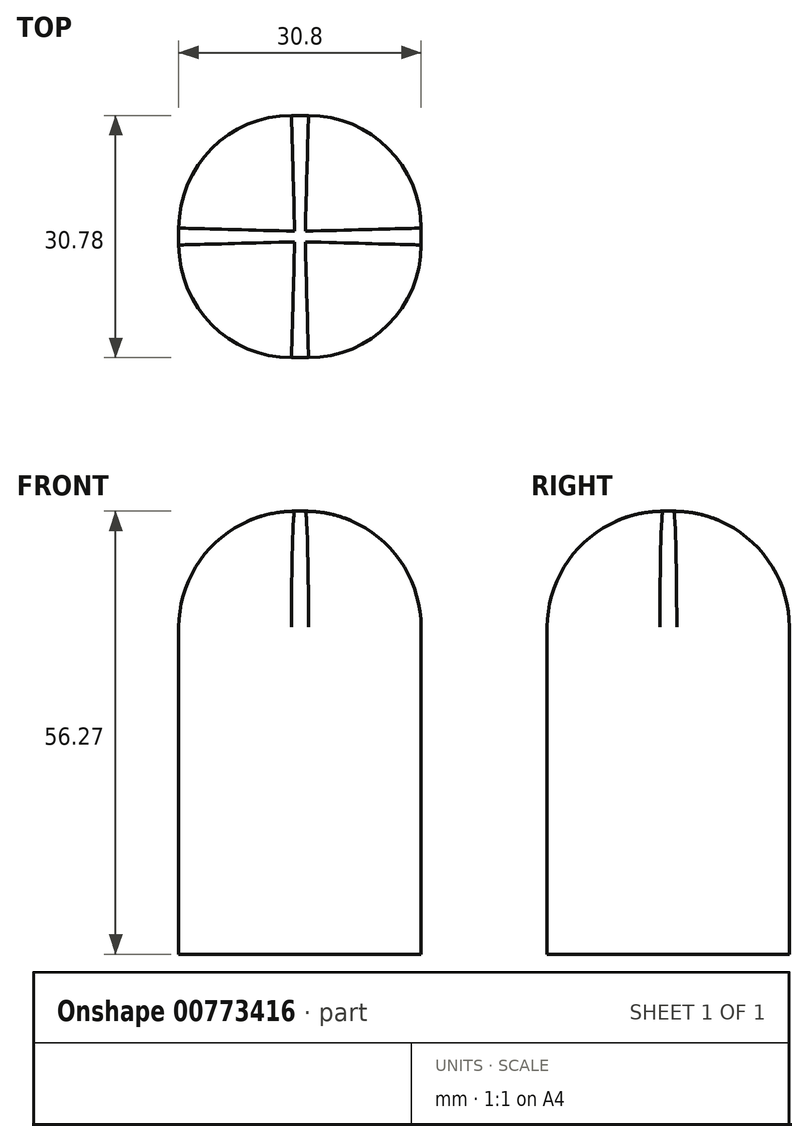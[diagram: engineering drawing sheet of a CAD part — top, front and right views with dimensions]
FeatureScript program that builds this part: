
annotation { "Feature Type Name" : "Feature", "Feature Type Description" : "" }
export const myFeature = defineFeature(function(context is Context, id is Id, definition is map)
    precondition{}
    {
        {
            var Q0;
            Q0=qCreatedBy(makeId("Front.planeOp"),FACE);
            var sketch = newSketch(context, id + "F0", { "sketchPlane" : qUnion([Q0])});
            skLineSegment(sketch, "E0", {"start": v(0, 0) * mm, "end": v(0, 56.27) * mm});
            skLineSegment(sketch, "E1", {"start": v(0, 56.27) * mm, "end": v(15.4, 56.27) * mm});
            skLineSegment(sketch, "E2", {"start": v(15.4, 56.27) * mm, "end": v(15.4, 0) * mm});
            skLineSegment(sketch, "E3", {"start": v(15.4, 0) * mm, "end": v(0, 0) * mm});
            skLineSegment(sketch, "E4", {"start": v(0, 0) * mm, "end": v(-15.4, 0) * mm});
            skLineSegment(sketch, "E5", {"start": v(-15.4, 0) * mm, "end": v(-15.4, 56.27) * mm});
            skLineSegment(sketch, "E6", {"start": v(-15.4, 56.27) * mm, "end": v(0, 56.27) * mm});
            skSolve(sketch);
        }
        {
            var Q0;
            Q0=makeQuery(id+"F0.imprint","IMPRINT",FACE,{"disambiguationData":[TD([[makeQuery(id+"F0.imprint","IMPRINT",EDGE,{"derivedFrom":sQuery(id+"F0.wireOp",EDGE,"E0")}),1.0]])]});
            var Q1;
            Q1=makeQuery(id+"F0.imprint","IMPRINT",FACE,{"disambiguationData":[TD([[makeQuery(id+"F0.imprint","IMPRINT",EDGE,{"derivedFrom":sQuery(id+"F0.wireOp",EDGE,"E0")}),-1.0]])]});
            extrude(context, id + "F1", {"entities" : qUnion([Q0, Q1]), "depth" : 30.78 * mm, "offsetDistance" : 25.4 * mm});
        }
        {
            var Q0;
            Q0=makeQuery(id+"F1.opExtrude","CAP_EDGE",EDGE,{"disambiguationData":[OSD([sQuery(id+"F0.wireOp",EDGE,"E1"),sQuery(id+"F0.wireOp",EDGE,"E6")])],"isStart":false});
            var Q1;
            Q1=makeQuery(id+"F1.opExtrude","SWEPT_EDGE",EDGE,{"disambiguationData":[OSD([sQuery(id+"F0.wireOp",EDGE,"E1"),sQuery(id+"F0.wireOp",EDGE,"E2")])]});
            var Q2;
            Q2=makeQuery(id+"F1.opExtrude","CAP_EDGE",EDGE,{"disambiguationData":[OSD([sQuery(id+"F0.wireOp",EDGE,"E1"),sQuery(id+"F0.wireOp",EDGE,"E6")])],"isStart":true});
            var Q3;
            Q3=makeQuery(id+"F1.opExtrude","SWEPT_EDGE",EDGE,{"disambiguationData":[OSD([sQuery(id+"F0.wireOp",EDGE,"E5"),sQuery(id+"F0.wireOp",EDGE,"E6")])]});
            fillet(context, id + "F2", {"entities" : qUnion([Q0, Q1, Q2, Q3]), "radius" : 14.72 * mm, "tangentPropagation" : true, "allowEdgeOverflow" : false});
        }
        {
            var Q0;
            {var subQ0=sQuery(id+"F0.wireOp",EDGE,"E6");Q0=makeQuery(id+"F2.opFillet","BLEND_EDGE",EDGE,{"blendedFrom":[makeQuery(id+"F1.opExtrude","SWEPT_EDGE",EDGE,{"disambiguationData":[OSD([sQuery(id+"F0.wireOp",EDGE,"E5"),subQ0])]}),makeQuery(id+"F1.opExtrude","CAP_EDGE",EDGE,{"disambiguationData":[OSD([sQuery(id+"F0.wireOp",EDGE,"E1"),subQ0])],"isStart":true})],"blendedInto":[]});}
            var Q1;
            {var subQ0=sQuery(id+"F0.wireOp",EDGE,"E1");Q1=makeQuery(id+"F2.opFillet","BLEND_EDGE",EDGE,{"blendedFrom":[makeQuery(id+"F1.opExtrude","SWEPT_EDGE",EDGE,{"disambiguationData":[OSD([subQ0,sQuery(id+"F0.wireOp",EDGE,"E2")])]}),makeQuery(id+"F1.opExtrude","CAP_EDGE",EDGE,{"disambiguationData":[OSD([subQ0,sQuery(id+"F0.wireOp",EDGE,"E6")])],"isStart":true})],"blendedInto":[]});}
            var Q2;
            {var subQ0=sQuery(id+"F0.wireOp",EDGE,"E1");Q2=makeQuery(id+"F2.opFillet","BLEND_EDGE",EDGE,{"blendedFrom":[makeQuery(id+"F1.opExtrude","SWEPT_EDGE",EDGE,{"disambiguationData":[OSD([subQ0,sQuery(id+"F0.wireOp",EDGE,"E2")])]}),makeQuery(id+"F1.opExtrude","CAP_EDGE",EDGE,{"disambiguationData":[OSD([subQ0,sQuery(id+"F0.wireOp",EDGE,"E6")])],"isStart":false})],"blendedInto":[]});}
            var Q3;
            {var subQ0=sQuery(id+"F0.wireOp",EDGE,"E6");Q3=makeQuery(id+"F2.opFillet","BLEND_EDGE",EDGE,{"blendedFrom":[makeQuery(id+"F1.opExtrude","SWEPT_EDGE",EDGE,{"disambiguationData":[OSD([sQuery(id+"F0.wireOp",EDGE,"E5"),subQ0])]}),makeQuery(id+"F1.opExtrude","CAP_EDGE",EDGE,{"disambiguationData":[OSD([sQuery(id+"F0.wireOp",EDGE,"E1"),subQ0])],"isStart":false})],"blendedInto":[]});}
            fillet(context, id + "F3", {"entities" : qUnion([Q0, Q1, Q2, Q3]), "radius" : 14.32 * mm, "tangentPropagation" : true, "allowEdgeOverflow" : false});
        }
    });
